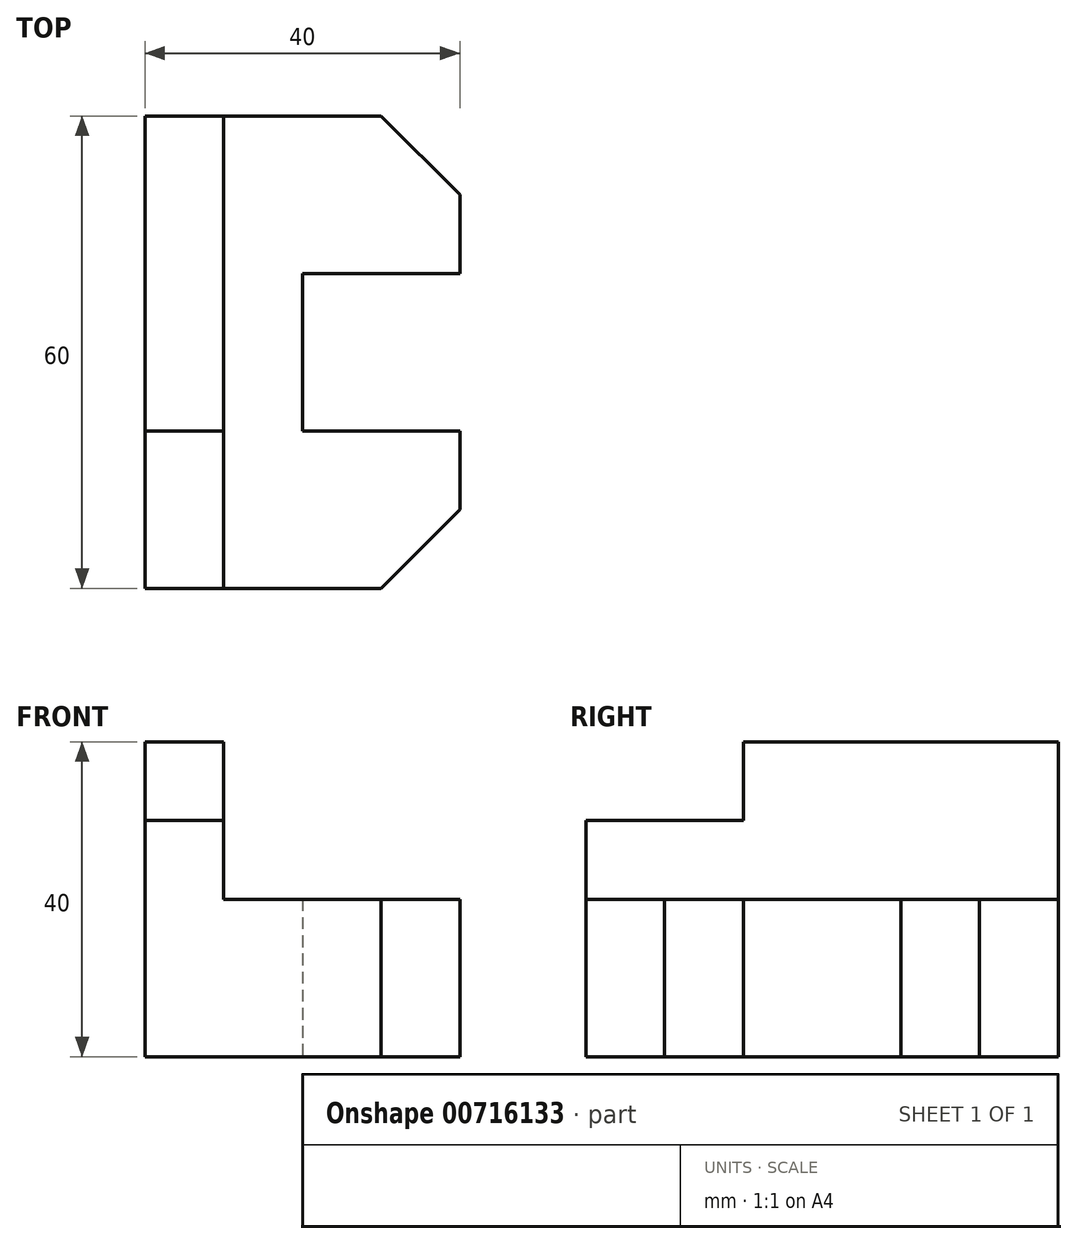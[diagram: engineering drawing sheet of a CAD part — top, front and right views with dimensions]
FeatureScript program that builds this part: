
annotation { "Feature Type Name" : "Feature", "Feature Type Description" : "" }
export const myFeature = defineFeature(function(context is Context, id is Id, definition is map)
    precondition{}
    {
        {
            var Q0;
            Q0=qCreatedBy(makeId("Top.planeOp"),FACE);
            var sketch = newSketch(context, id + "F0", { "sketchPlane" : qUnion([Q0])});
            skLineSegment(sketch, "E0", {"start": v(0, -30) * mm, "end": v(0, 30) * mm});
            skLineSegment(sketch, "E1", {"start": v(0, 30) * mm, "end": v(40, 30) * mm});
            skLineSegment(sketch, "E2", {"start": v(40, 30) * mm, "end": v(40, 10) * mm});
            skLineSegment(sketch, "E3", {"start": v(40, 10) * mm, "end": v(20, 10) * mm});
            skLineSegment(sketch, "E4", {"start": v(20, 10) * mm, "end": v(20, -10) * mm});
            skLineSegment(sketch, "E5", {"start": v(20, -10) * mm, "end": v(40, -10) * mm});
            skLineSegment(sketch, "E6", {"start": v(40, -10) * mm, "end": v(40, -30) * mm});
            skLineSegment(sketch, "E7", {"start": v(40, -30) * mm, "end": v(0, -30) * mm});
            skSolve(sketch);
        }
        {
            var Q0;
            Q0 = qSketchRegion(id + "F0", true);
            extrude(context, id + "F1", {"entities" : qUnion([Q0]), "depth" : 20 * mm, "offsetDistance" : 25 * mm});
        }
        {
            var Q0;
            Q0=makeQuery(id+"F1.opExtrude","SWEPT_EDGE",EDGE,{"disambiguationData":[OSD([sQuery(id+"F0.wireOp",EDGE,"E6"),sQuery(id+"F0.wireOp",EDGE,"E7")])]});
            var Q1;
            Q1=makeQuery(id+"F1.opExtrude","SWEPT_EDGE",EDGE,{"disambiguationData":[OSD([sQuery(id+"F0.wireOp",EDGE,"E1"),sQuery(id+"F0.wireOp",EDGE,"E2")])]});
            chamfer(context, id + "F2", {"entities" : qUnion([Q0, Q1]), "width" : 10 * mm, "tangentPropagation" : true});
        }
        {
            var Q0;
            Q0=makeQuery(id+"F1.opExtrude","SWEPT_FACE",FACE,{"disambiguationData":[OSD([sQuery(id+"F0.wireOp",EDGE,"E0")])]});
            var sketch = newSketch(context, id + "F3", { "sketchPlane" : qUnion([Q0])});
            skLineSegment(sketch, "E8", {"start": v(-30, 20) * mm, "end": v(-30, 40) * mm});
            skLineSegment(sketch, "E9", {"start": v(-30, 40) * mm, "end": v(10, 40) * mm});
            skLineSegment(sketch, "E10", {"start": v(10, 40) * mm, "end": v(10, 30) * mm});
            skLineSegment(sketch, "E11", {"start": v(10, 30) * mm, "end": v(30, 30) * mm});
            skLineSegment(sketch, "E12", {"start": v(30, 30) * mm, "end": v(30, 20) * mm});
            skLineSegment(sketch, "E13", {"start": v(30, 20) * mm, "end": v(-30, 20) * mm});
            skSolve(sketch);
        }
        {
            var Q0;
            Q0=makeQuery(id+"F3.imprint","IMPRINT",FACE,{"disambiguationData":[TD([[makeQuery(id+"F3.imprint","IMPRINT",EDGE,{"derivedFrom":sQuery(id+"F3.wireOp",EDGE,"E8")}),-1.0]])]});
            extrude(context, id + "F4", {"entities" : qUnion([Q0]), "operationType" : NewBodyOperationType.ADD, "oppositeDirection" : true, "depth" : 10 * mm, "offsetDistance" : 25 * mm});
        }
    });
